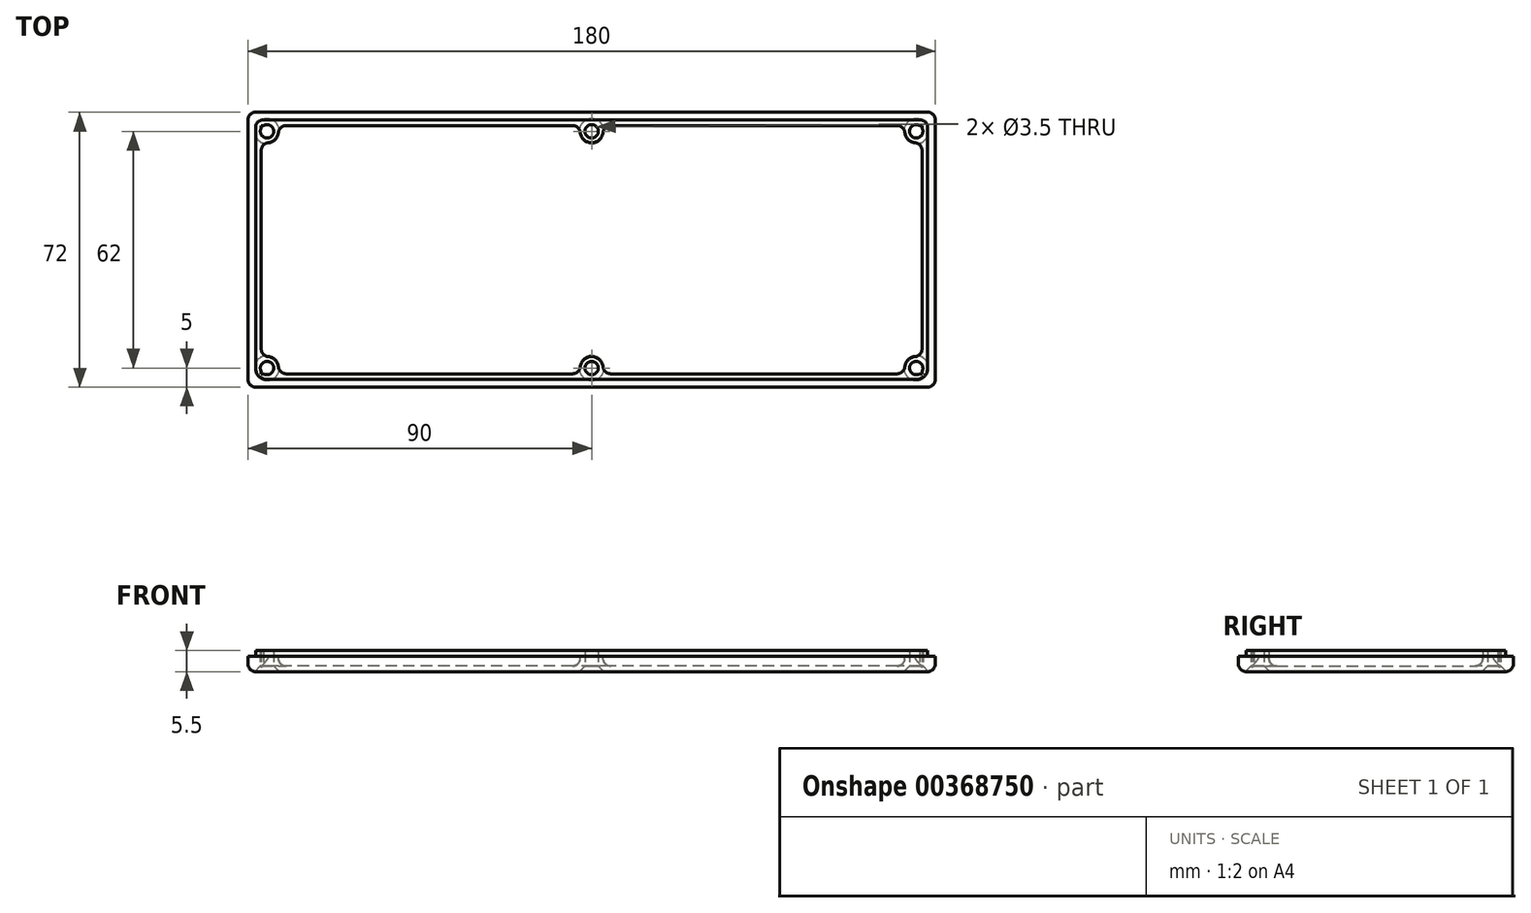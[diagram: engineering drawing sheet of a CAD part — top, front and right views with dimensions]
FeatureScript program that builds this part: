
annotation { "Feature Type Name" : "Feature", "Feature Type Description" : "" }
export const myFeature = defineFeature(function(context is Context, id is Id, definition is map)
    precondition{}
    {
        {
            var Q0;
            Q0=qCreatedBy(makeId("Top.planeOp"),FACE);
            var sketch = newSketch(context, id + "F0", { "sketchPlane" : qUnion([Q0])});
            skLineSegment(sketch, "E0.bottom", {"start": v(-90, 36) * mm, "end": v(90, 36) * mm});
            skLineSegment(sketch, "E0.top", {"start": v(-90, -36) * mm, "end": v(90, -36) * mm});
            skLineSegment(sketch, "E0.left", {"start": v(-90, 36) * mm, "end": v(-90, -36) * mm});
            skLineSegment(sketch, "E0.right", {"start": v(90, 36) * mm, "end": v(90, -36) * mm});
            skPoint(sketch, "E0.middle", {"position": v(0, 0) * mm});
            skLineSegment(sketch, "E1.bottom", {"start": v(-88, 34) * mm, "end": v(88, 34) * mm});
            skLineSegment(sketch, "E1.top", {"start": v(-88, -34) * mm, "end": v(88, -34) * mm});
            skLineSegment(sketch, "E1.left", {"start": v(-88, 34) * mm, "end": v(-88, -34) * mm});
            skLineSegment(sketch, "E1.right", {"start": v(88, 34) * mm, "end": v(88, -34) * mm});
            skLineSegment(sketch, "E2.bottom", {"start": v(-86.5, 32.5) * mm, "end": v(86.5, 32.5) * mm});
            skLineSegment(sketch, "E2.top", {"start": v(-86.5, -32.5) * mm, "end": v(86.5, -32.5) * mm});
            skLineSegment(sketch, "E2.left", {"start": v(-86.5, 32.5) * mm, "end": v(-86.5, -32.5) * mm});
            skLineSegment(sketch, "E2.right", {"start": v(86.5, 32.5) * mm, "end": v(86.5, -32.5) * mm});
            skCircle(sketch, "E3", {"center": v(-85, 31) * mm, "radius": 1.75 * mm});
            skCircle(sketch, "E4.MirrorC", {"center": v(85, 31) * mm, "radius": 1.75 * mm});
            skCircle(sketch, "E5.MirrorC", {"center": v(-85, -31) * mm, "radius": 1.75 * mm});
            skCircle(sketch, "E6.MirrorC", {"center": v(85, -31) * mm, "radius": 1.75 * mm});
            skCircle(sketch, "E7", {"center": v(0, 31) * mm, "radius": 1.75 * mm});
            skCircle(sketch, "E8.MirrorC", {"center": v(0, -31) * mm, "radius": 1.75 * mm});
            skCircle(sketch, "E9", {"center": v(-85, 31) * mm, "radius": 3 * mm});
            skCircle(sketch, "E10.MirrorC", {"center": v(85, 31) * mm, "radius": 3 * mm});
            skCircle(sketch, "E11.MirrorC", {"center": v(-85, -31) * mm, "radius": 3 * mm});
            skCircle(sketch, "E12.MirrorC", {"center": v(85, -31) * mm, "radius": 3 * mm});
            skCircle(sketch, "E13", {"center": v(0, 31) * mm, "radius": 3 * mm});
            skCircle(sketch, "E14.MirrorC", {"center": v(0, -31) * mm, "radius": 3 * mm});
            skSolve(sketch);
        }
        {
            var Q0;
            {var subQ5=sQuery(id+"F0.wireOp",EDGE,"E9");var subQ12=sQuery(id+"F0.wireOp",EDGE,"E2.bottom");var subQ15=makeQuery(id+"F0.imprint","INTERSECT",VERTEX,{"derivedFrom":[subQ12,subQ5]});Q0=makeQuery(id+"F0.imprint","IMPRINT",FACE,{"disambiguationData":[TD([[makeQuery(id+"F0.imprint","IMPRINT",EDGE,{"disambiguationData":[TD([[subQ15,-1.0]])],"derivedFrom":subQ12}),-1.0]])]});}
            var Q1;
            {var subQ0=sQuery(id+"F0.wireOp",EDGE,"E9");var subQ1=sQuery(id+"F0.wireOp",EDGE,"E1.bottom");var subQ2=makeQuery(id+"F0.imprint","INTERSECT",VERTEX,{"derivedFrom":[subQ1,subQ0]});Q1=makeQuery(id+"F0.imprint","IMPRINT",FACE,{"disambiguationData":[TD([[makeQuery(id+"F0.imprint","IMPRINT",EDGE,{"disambiguationData":[TD([[subQ2,-1.0]])],"derivedFrom":subQ1}),-1.0]])]});}
            var Q2;
            Q2=makeQuery(id+"F0.imprint","IMPRINT",FACE,{"disambiguationData":[TD([[makeQuery(id+"F0.imprint","IMPRINT",EDGE,{"derivedFrom":sQuery(id+"F0.wireOp",EDGE,"E0.bottom")}),-1.0]])]});
            var Q3;
            {var subQ0=sQuery(id+"F0.wireOp",EDGE,"E13");var subQ1=sQuery(id+"F0.wireOp",EDGE,"E1.bottom");var subQ2=makeQuery(id+"F0.imprint","INTERSECT",VERTEX,{"derivedFrom":[subQ1,subQ0]});Q3=makeQuery(id+"F0.imprint","IMPRINT",FACE,{"disambiguationData":[TD([[makeQuery(id+"F0.imprint","IMPRINT",EDGE,{"disambiguationData":[TD([[subQ2,-1.0]])],"derivedFrom":subQ1}),-1.0]])]});}
            var Q4;
            {var subQ0=sQuery(id+"F0.wireOp",EDGE,"E13");var subQ1=sQuery(id+"F0.wireOp",EDGE,"E2.bottom");var subQ2=makeQuery(id+"F0.imprint","INTERSECT",VERTEX,{"disambiguationData":[OD(0.0)],"derivedFrom":[subQ1,subQ0]});Q4=makeQuery(id+"F0.imprint","IMPRINT",FACE,{"disambiguationData":[TD([[makeQuery(id+"F0.imprint","IMPRINT",EDGE,{"disambiguationData":[TD([[subQ2,-1.0]])],"derivedFrom":subQ1}),-1.0]])]});}
            var Q5;
            {var subQ0=sQuery(id+"F0.wireOp",EDGE,"E13");var subQ2=sQuery(id+"F0.wireOp",EDGE,"E2.bottom");var subQ7=makeQuery(id+"F0.imprint","INTERSECT",VERTEX,{"disambiguationData":[OD(0.0)],"derivedFrom":[subQ2,subQ0]});Q5=makeQuery(id+"F0.imprint","IMPRINT",FACE,{"disambiguationData":[TD([[makeQuery(id+"F0.imprint","IMPRINT",EDGE,{"disambiguationData":[TD([[subQ7,-1.0]])],"derivedFrom":subQ2}),1.0]])]});}
            var Q6;
            {var subQ0=sQuery(id+"F0.wireOp",EDGE,"E9");var subQ1=sQuery(id+"F0.wireOp",EDGE,"E1.left");var subQ2=makeQuery(id+"F0.imprint","INTERSECT",VERTEX,{"derivedFrom":[subQ1,subQ0]});Q6=makeQuery(id+"F0.imprint","IMPRINT",FACE,{"disambiguationData":[TD([[makeQuery(id+"F0.imprint","IMPRINT",EDGE,{"disambiguationData":[TD([[subQ2,-1.0]])],"derivedFrom":subQ1}),1.0]])]});}
            var Q7;
            {var subQ1=sQuery(id+"F0.wireOp",EDGE,"E2.left");var subQ5=sQuery(id+"F0.wireOp",EDGE,"E2.bottom");var subQ10=makeQuery(id+"F0.imprint","INTERSECT",VERTEX,{"derivedFrom":[subQ5,subQ1]});Q7=makeQuery(id+"F0.imprint","IMPRINT",FACE,{"disambiguationData":[TD([[makeQuery(id+"F0.imprint","IMPRINT",EDGE,{"disambiguationData":[TD([[subQ10,-1.0]])],"derivedFrom":subQ5}),1.0]])]});}
            var Q8;
            {var subQ0=sQuery(id+"F0.wireOp",EDGE,"E3");var subQ1=sQuery(id+"F0.wireOp",EDGE,"E2.bottom");var subQ2=makeQuery(id+"F0.imprint","INTERSECT",VERTEX,{"disambiguationData":[OD(1.0)],"derivedFrom":[subQ1,subQ0]});Q8=makeQuery(id+"F0.imprint","IMPRINT",FACE,{"disambiguationData":[TD([[makeQuery(id+"F0.imprint","IMPRINT",EDGE,{"disambiguationData":[TD([[subQ2,-1.0]])],"derivedFrom":subQ1}),-1.0]])]});}
            var Q9;
            {var subQ0=sQuery(id+"F0.wireOp",EDGE,"E1.left");var subQ1=sQuery(id+"F0.wireOp",EDGE,"E1.bottom");var subQ2=makeQuery(id+"F0.imprint","INTERSECT",VERTEX,{"derivedFrom":[subQ1,subQ0]});Q9=makeQuery(id+"F0.imprint","IMPRINT",FACE,{"disambiguationData":[TD([[makeQuery(id+"F0.imprint","IMPRINT",EDGE,{"disambiguationData":[TD([[subQ2,-1.0]])],"derivedFrom":subQ1}),-1.0]])]});}
            var Q10;
            {var subQ0=sQuery(id+"F0.wireOp",EDGE,"E5.MirrorC");var subQ1=sQuery(id+"F0.wireOp",EDGE,"E2.top");var subQ2=makeQuery(id+"F0.imprint","INTERSECT",VERTEX,{"disambiguationData":[OD(1.0)],"derivedFrom":[subQ1,subQ0]});Q10=makeQuery(id+"F0.imprint","IMPRINT",FACE,{"disambiguationData":[TD([[makeQuery(id+"F0.imprint","IMPRINT",EDGE,{"disambiguationData":[TD([[subQ2,-1.0]])],"derivedFrom":subQ1}),1.0]])]});}
            var Q11;
            {var subQ0=sQuery(id+"F0.wireOp",EDGE,"E2.left");var subQ1=sQuery(id+"F0.wireOp",EDGE,"E2.top");var subQ2=makeQuery(id+"F0.imprint","INTERSECT",VERTEX,{"derivedFrom":[subQ1,subQ0]});Q11=makeQuery(id+"F0.imprint","IMPRINT",FACE,{"disambiguationData":[TD([[makeQuery(id+"F0.imprint","IMPRINT",EDGE,{"disambiguationData":[TD([[subQ2,-1.0]])],"derivedFrom":subQ1}),-1.0]])]});}
            var Q12;
            {var subQ0=sQuery(id+"F0.wireOp",EDGE,"E1.left");var subQ1=sQuery(id+"F0.wireOp",EDGE,"E1.top");var subQ2=makeQuery(id+"F0.imprint","INTERSECT",VERTEX,{"derivedFrom":[subQ1,subQ0]});Q12=makeQuery(id+"F0.imprint","IMPRINT",FACE,{"disambiguationData":[TD([[makeQuery(id+"F0.imprint","IMPRINT",EDGE,{"disambiguationData":[TD([[subQ2,-1.0]])],"derivedFrom":subQ1}),1.0]])]});}
            var Q13;
            {var subQ0=sQuery(id+"F0.wireOp",EDGE,"E11.MirrorC");var subQ1=sQuery(id+"F0.wireOp",EDGE,"E1.top");var subQ2=makeQuery(id+"F0.imprint","INTERSECT",VERTEX,{"derivedFrom":[subQ1,subQ0]});Q13=makeQuery(id+"F0.imprint","IMPRINT",FACE,{"disambiguationData":[TD([[makeQuery(id+"F0.imprint","IMPRINT",EDGE,{"disambiguationData":[TD([[subQ2,-1.0]])],"derivedFrom":subQ1}),1.0]])]});}
            var Q14;
            {var subQ1=sQuery(id+"F0.wireOp",EDGE,"E2.top");var subQ4=sQuery(id+"F0.wireOp",EDGE,"E14.MirrorC");var subQ6=makeQuery(id+"F0.imprint","INTERSECT",VERTEX,{"disambiguationData":[OD(0.0)],"derivedFrom":[subQ1,subQ4]});Q14=makeQuery(id+"F0.imprint","IMPRINT",FACE,{"disambiguationData":[TD([[makeQuery(id+"F0.imprint","IMPRINT",EDGE,{"disambiguationData":[TD([[subQ6,-1.0]])],"derivedFrom":subQ1}),-1.0]])]});}
            var Q15;
            {var subQ0=sQuery(id+"F0.wireOp",EDGE,"E14.MirrorC");var subQ1=sQuery(id+"F0.wireOp",EDGE,"E2.top");var subQ2=makeQuery(id+"F0.imprint","INTERSECT",VERTEX,{"disambiguationData":[OD(0.0)],"derivedFrom":[subQ1,subQ0]});Q15=makeQuery(id+"F0.imprint","IMPRINT",FACE,{"disambiguationData":[TD([[makeQuery(id+"F0.imprint","IMPRINT",EDGE,{"disambiguationData":[TD([[subQ2,-1.0]])],"derivedFrom":subQ1}),1.0]])]});}
            var Q16;
            {var subQ0=sQuery(id+"F0.wireOp",EDGE,"E14.MirrorC");var subQ1=sQuery(id+"F0.wireOp",EDGE,"E1.top");var subQ2=makeQuery(id+"F0.imprint","INTERSECT",VERTEX,{"derivedFrom":[subQ1,subQ0]});Q16=makeQuery(id+"F0.imprint","IMPRINT",FACE,{"disambiguationData":[TD([[makeQuery(id+"F0.imprint","IMPRINT",EDGE,{"disambiguationData":[TD([[subQ2,-1.0]])],"derivedFrom":subQ1}),1.0]])]});}
            var Q17;
            {var subQ1=sQuery(id+"F0.wireOp",EDGE,"E2.top");var subQ5=sQuery(id+"F0.wireOp",EDGE,"E12.MirrorC");var subQ7=makeQuery(id+"F0.imprint","INTERSECT",VERTEX,{"derivedFrom":[subQ1,subQ5]});Q17=makeQuery(id+"F0.imprint","IMPRINT",FACE,{"disambiguationData":[TD([[makeQuery(id+"F0.imprint","IMPRINT",EDGE,{"disambiguationData":[TD([[subQ7,-1.0]])],"derivedFrom":subQ1}),-1.0]])]});}
            var Q18;
            {var subQ0=sQuery(id+"F0.wireOp",EDGE,"E10.MirrorC");var subQ1=sQuery(id+"F0.wireOp",EDGE,"E1.right");var subQ2=makeQuery(id+"F0.imprint","INTERSECT",VERTEX,{"derivedFrom":[subQ1,subQ0]});Q18=makeQuery(id+"F0.imprint","IMPRINT",FACE,{"disambiguationData":[TD([[makeQuery(id+"F0.imprint","IMPRINT",EDGE,{"disambiguationData":[TD([[subQ2,-1.0]])],"derivedFrom":subQ1}),-1.0]])]});}
            var Q19;
            {var subQ0=sQuery(id+"F0.wireOp",EDGE,"E12.MirrorC");var subQ1=sQuery(id+"F0.wireOp",EDGE,"E2.top");var subQ2=makeQuery(id+"F0.imprint","INTERSECT",VERTEX,{"derivedFrom":[subQ1,subQ0]});Q19=makeQuery(id+"F0.imprint","IMPRINT",FACE,{"disambiguationData":[TD([[makeQuery(id+"F0.imprint","IMPRINT",EDGE,{"disambiguationData":[TD([[subQ2,-1.0]])],"derivedFrom":subQ1}),1.0]])]});}
            var Q20;
            {var subQ0=sQuery(id+"F0.wireOp",EDGE,"E10.MirrorC");var subQ1=sQuery(id+"F0.wireOp",EDGE,"E2.bottom");var subQ2=makeQuery(id+"F0.imprint","INTERSECT",VERTEX,{"derivedFrom":[subQ1,subQ0]});Q20=makeQuery(id+"F0.imprint","IMPRINT",FACE,{"disambiguationData":[TD([[makeQuery(id+"F0.imprint","IMPRINT",EDGE,{"disambiguationData":[TD([[subQ2,-1.0]])],"derivedFrom":subQ1}),-1.0]])]});}
            var Q21;
            {var subQ3=sQuery(id+"F0.wireOp",EDGE,"E10.MirrorC");var subQ6=sQuery(id+"F0.wireOp",EDGE,"E2.bottom");var subQ11=makeQuery(id+"F0.imprint","INTERSECT",VERTEX,{"derivedFrom":[subQ6,subQ3]});Q21=makeQuery(id+"F0.imprint","IMPRINT",FACE,{"disambiguationData":[TD([[makeQuery(id+"F0.imprint","IMPRINT",EDGE,{"disambiguationData":[TD([[subQ11,-1.0]])],"derivedFrom":subQ6}),1.0]])]});}
            var Q22;
            {var subQ0=sQuery(id+"F0.wireOp",EDGE,"E1.right");var subQ1=sQuery(id+"F0.wireOp",EDGE,"E1.bottom");var subQ2=makeQuery(id+"F0.imprint","INTERSECT",VERTEX,{"derivedFrom":[subQ1,subQ0]});Q22=makeQuery(id+"F0.imprint","IMPRINT",FACE,{"disambiguationData":[TD([[makeQuery(id+"F0.imprint","IMPRINT",EDGE,{"disambiguationData":[TD([[subQ2,1.0]])],"derivedFrom":subQ1}),-1.0]])]});}
            var Q23;
            {var subQ0=sQuery(id+"F0.wireOp",EDGE,"E1.right");var subQ1=sQuery(id+"F0.wireOp",EDGE,"E1.top");var subQ2=makeQuery(id+"F0.imprint","INTERSECT",VERTEX,{"derivedFrom":[subQ1,subQ0]});Q23=makeQuery(id+"F0.imprint","IMPRINT",FACE,{"disambiguationData":[TD([[makeQuery(id+"F0.imprint","IMPRINT",EDGE,{"disambiguationData":[TD([[subQ2,1.0]])],"derivedFrom":subQ1}),1.0]])]});}
            extrude(context, id + "F1", {"entities" : qUnion([Q0, Q1, Q2, Q3, Q4, Q5, Q6, Q7, Q8, Q9, Q10, Q11, Q12, Q13, Q14, Q15, Q16, Q17, Q18, Q19, Q20, Q21, Q22, Q23]), "depth" : 1.5 * mm, "offsetDistance" : 25 * mm});
        }
        {
            var Q0;
            Q0=makeQuery(id+"F0.imprint","IMPRINT",FACE,{"disambiguationData":[TD([[makeQuery(id+"F0.imprint","IMPRINT",EDGE,{"derivedFrom":sQuery(id+"F0.wireOp",EDGE,"E0.bottom")}),-1.0]])]});
            var Q1;
            {var subQ0=sQuery(id+"F0.wireOp",EDGE,"E1.left");var subQ1=sQuery(id+"F0.wireOp",EDGE,"E1.bottom");var subQ2=makeQuery(id+"F0.imprint","INTERSECT",VERTEX,{"derivedFrom":[subQ1,subQ0]});Q1=makeQuery(id+"F0.imprint","IMPRINT",FACE,{"disambiguationData":[TD([[makeQuery(id+"F0.imprint","IMPRINT",EDGE,{"disambiguationData":[TD([[subQ2,-1.0]])],"derivedFrom":subQ1}),-1.0]])]});}
            var Q2;
            {var subQ0=sQuery(id+"F0.wireOp",EDGE,"E1.left");var subQ1=sQuery(id+"F0.wireOp",EDGE,"E1.top");var subQ2=makeQuery(id+"F0.imprint","INTERSECT",VERTEX,{"derivedFrom":[subQ1,subQ0]});Q2=makeQuery(id+"F0.imprint","IMPRINT",FACE,{"disambiguationData":[TD([[makeQuery(id+"F0.imprint","IMPRINT",EDGE,{"disambiguationData":[TD([[subQ2,-1.0]])],"derivedFrom":subQ1}),1.0]])]});}
            var Q3;
            {var subQ0=sQuery(id+"F0.wireOp",EDGE,"E1.right");var subQ1=sQuery(id+"F0.wireOp",EDGE,"E1.top");var subQ2=makeQuery(id+"F0.imprint","INTERSECT",VERTEX,{"derivedFrom":[subQ1,subQ0]});Q3=makeQuery(id+"F0.imprint","IMPRINT",FACE,{"disambiguationData":[TD([[makeQuery(id+"F0.imprint","IMPRINT",EDGE,{"disambiguationData":[TD([[subQ2,1.0]])],"derivedFrom":subQ1}),1.0]])]});}
            var Q4;
            {var subQ0=sQuery(id+"F0.wireOp",EDGE,"E1.right");var subQ1=sQuery(id+"F0.wireOp",EDGE,"E1.bottom");var subQ2=makeQuery(id+"F0.imprint","INTERSECT",VERTEX,{"derivedFrom":[subQ1,subQ0]});Q4=makeQuery(id+"F0.imprint","IMPRINT",FACE,{"disambiguationData":[TD([[makeQuery(id+"F0.imprint","IMPRINT",EDGE,{"disambiguationData":[TD([[subQ2,1.0]])],"derivedFrom":subQ1}),-1.0]])]});}
            extrude(context, id + "F2", {"entities" : qUnion([Q0, Q1, Q2, Q3, Q4]), "operationType" : NewBodyOperationType.ADD, "depth" : 4 * mm, "offsetDistance" : 25 * mm});
        }
        {
            var Q0;
            Q0=makeQuery(id+"F0.imprint","IMPRINT",FACE,{"disambiguationData":[TD([[makeQuery(id+"F0.imprint","IMPRINT",EDGE,{"derivedFrom":sQuery(id+"F0.wireOp",EDGE,"E1.bottom")}),-1.0]])]});
            var Q1;
            {var subQ0=sQuery(id+"F0.wireOp",EDGE,"E10.MirrorC");var subQ1=sQuery(id+"F0.wireOp",EDGE,"E2.bottom");var subQ2=makeQuery(id+"F0.imprint","INTERSECT",VERTEX,{"derivedFrom":[subQ1,subQ0]});Q1=makeQuery(id+"F0.imprint","IMPRINT",FACE,{"disambiguationData":[TD([[makeQuery(id+"F0.imprint","IMPRINT",EDGE,{"disambiguationData":[TD([[subQ2,-1.0]])],"derivedFrom":subQ1}),-1.0]])]});}
            var Q2;
            {var subQ3=sQuery(id+"F0.wireOp",EDGE,"E10.MirrorC");var subQ6=sQuery(id+"F0.wireOp",EDGE,"E2.bottom");var subQ11=makeQuery(id+"F0.imprint","INTERSECT",VERTEX,{"derivedFrom":[subQ6,subQ3]});Q2=makeQuery(id+"F0.imprint","IMPRINT",FACE,{"disambiguationData":[TD([[makeQuery(id+"F0.imprint","IMPRINT",EDGE,{"disambiguationData":[TD([[subQ11,-1.0]])],"derivedFrom":subQ6}),1.0]])]});}
            var Q3;
            {var subQ0=sQuery(id+"F0.wireOp",EDGE,"E10.MirrorC");var subQ1=sQuery(id+"F0.wireOp",EDGE,"E1.right");var subQ2=makeQuery(id+"F0.imprint","INTERSECT",VERTEX,{"derivedFrom":[subQ1,subQ0]});Q3=makeQuery(id+"F0.imprint","IMPRINT",FACE,{"disambiguationData":[TD([[makeQuery(id+"F0.imprint","IMPRINT",EDGE,{"disambiguationData":[TD([[subQ2,-1.0]])],"derivedFrom":subQ1}),-1.0]])]});}
            var Q4;
            {var subQ0=sQuery(id+"F0.wireOp",EDGE,"E13");var subQ1=sQuery(id+"F0.wireOp",EDGE,"E1.bottom");var subQ2=makeQuery(id+"F0.imprint","INTERSECT",VERTEX,{"derivedFrom":[subQ1,subQ0]});Q4=makeQuery(id+"F0.imprint","IMPRINT",FACE,{"disambiguationData":[TD([[makeQuery(id+"F0.imprint","IMPRINT",EDGE,{"disambiguationData":[TD([[subQ2,-1.0]])],"derivedFrom":subQ1}),-1.0]])]});}
            var Q5;
            {var subQ0=sQuery(id+"F0.wireOp",EDGE,"E13");var subQ2=sQuery(id+"F0.wireOp",EDGE,"E2.bottom");var subQ7=makeQuery(id+"F0.imprint","INTERSECT",VERTEX,{"disambiguationData":[OD(0.0)],"derivedFrom":[subQ2,subQ0]});Q5=makeQuery(id+"F0.imprint","IMPRINT",FACE,{"disambiguationData":[TD([[makeQuery(id+"F0.imprint","IMPRINT",EDGE,{"disambiguationData":[TD([[subQ7,-1.0]])],"derivedFrom":subQ2}),1.0]])]});}
            var Q6;
            {var subQ0=sQuery(id+"F0.wireOp",EDGE,"E13");var subQ1=sQuery(id+"F0.wireOp",EDGE,"E2.bottom");var subQ2=makeQuery(id+"F0.imprint","INTERSECT",VERTEX,{"disambiguationData":[OD(0.0)],"derivedFrom":[subQ1,subQ0]});Q6=makeQuery(id+"F0.imprint","IMPRINT",FACE,{"disambiguationData":[TD([[makeQuery(id+"F0.imprint","IMPRINT",EDGE,{"disambiguationData":[TD([[subQ2,-1.0]])],"derivedFrom":subQ1}),-1.0]])]});}
            var Q7;
            {var subQ0=sQuery(id+"F0.wireOp",EDGE,"E9");var subQ1=sQuery(id+"F0.wireOp",EDGE,"E1.bottom");var subQ2=makeQuery(id+"F0.imprint","INTERSECT",VERTEX,{"derivedFrom":[subQ1,subQ0]});Q7=makeQuery(id+"F0.imprint","IMPRINT",FACE,{"disambiguationData":[TD([[makeQuery(id+"F0.imprint","IMPRINT",EDGE,{"disambiguationData":[TD([[subQ2,-1.0]])],"derivedFrom":subQ1}),-1.0]])]});}
            var Q8;
            {var subQ0=sQuery(id+"F0.wireOp",EDGE,"E12.MirrorC");var subQ1=sQuery(id+"F0.wireOp",EDGE,"E2.top");var subQ2=makeQuery(id+"F0.imprint","INTERSECT",VERTEX,{"derivedFrom":[subQ1,subQ0]});Q8=makeQuery(id+"F0.imprint","IMPRINT",FACE,{"disambiguationData":[TD([[makeQuery(id+"F0.imprint","IMPRINT",EDGE,{"disambiguationData":[TD([[subQ2,-1.0]])],"derivedFrom":subQ1}),1.0]])]});}
            var Q9;
            {var subQ1=sQuery(id+"F0.wireOp",EDGE,"E2.top");var subQ5=sQuery(id+"F0.wireOp",EDGE,"E12.MirrorC");var subQ7=makeQuery(id+"F0.imprint","INTERSECT",VERTEX,{"derivedFrom":[subQ1,subQ5]});Q9=makeQuery(id+"F0.imprint","IMPRINT",FACE,{"disambiguationData":[TD([[makeQuery(id+"F0.imprint","IMPRINT",EDGE,{"disambiguationData":[TD([[subQ7,-1.0]])],"derivedFrom":subQ1}),-1.0]])]});}
            var Q10;
            {var subQ0=sQuery(id+"F0.wireOp",EDGE,"E14.MirrorC");var subQ1=sQuery(id+"F0.wireOp",EDGE,"E1.top");var subQ2=makeQuery(id+"F0.imprint","INTERSECT",VERTEX,{"derivedFrom":[subQ1,subQ0]});Q10=makeQuery(id+"F0.imprint","IMPRINT",FACE,{"disambiguationData":[TD([[makeQuery(id+"F0.imprint","IMPRINT",EDGE,{"disambiguationData":[TD([[subQ2,-1.0]])],"derivedFrom":subQ1}),1.0]])]});}
            var Q11;
            {var subQ0=sQuery(id+"F0.wireOp",EDGE,"E14.MirrorC");var subQ1=sQuery(id+"F0.wireOp",EDGE,"E2.top");var subQ2=makeQuery(id+"F0.imprint","INTERSECT",VERTEX,{"disambiguationData":[OD(0.0)],"derivedFrom":[subQ1,subQ0]});Q11=makeQuery(id+"F0.imprint","IMPRINT",FACE,{"disambiguationData":[TD([[makeQuery(id+"F0.imprint","IMPRINT",EDGE,{"disambiguationData":[TD([[subQ2,-1.0]])],"derivedFrom":subQ1}),1.0]])]});}
            var Q12;
            {var subQ1=sQuery(id+"F0.wireOp",EDGE,"E2.top");var subQ4=sQuery(id+"F0.wireOp",EDGE,"E14.MirrorC");var subQ6=makeQuery(id+"F0.imprint","INTERSECT",VERTEX,{"disambiguationData":[OD(0.0)],"derivedFrom":[subQ1,subQ4]});Q12=makeQuery(id+"F0.imprint","IMPRINT",FACE,{"disambiguationData":[TD([[makeQuery(id+"F0.imprint","IMPRINT",EDGE,{"disambiguationData":[TD([[subQ6,-1.0]])],"derivedFrom":subQ1}),-1.0]])]});}
            var Q13;
            {var subQ0=sQuery(id+"F0.wireOp",EDGE,"E11.MirrorC");var subQ1=sQuery(id+"F0.wireOp",EDGE,"E1.top");var subQ2=makeQuery(id+"F0.imprint","INTERSECT",VERTEX,{"derivedFrom":[subQ1,subQ0]});Q13=makeQuery(id+"F0.imprint","IMPRINT",FACE,{"disambiguationData":[TD([[makeQuery(id+"F0.imprint","IMPRINT",EDGE,{"disambiguationData":[TD([[subQ2,-1.0]])],"derivedFrom":subQ1}),1.0]])]});}
            var Q14;
            {var subQ0=sQuery(id+"F0.wireOp",EDGE,"E9");var subQ1=sQuery(id+"F0.wireOp",EDGE,"E1.left");var subQ2=makeQuery(id+"F0.imprint","INTERSECT",VERTEX,{"derivedFrom":[subQ1,subQ0]});Q14=makeQuery(id+"F0.imprint","IMPRINT",FACE,{"disambiguationData":[TD([[makeQuery(id+"F0.imprint","IMPRINT",EDGE,{"disambiguationData":[TD([[subQ2,-1.0]])],"derivedFrom":subQ1}),1.0]])]});}
            var Q15;
            {var subQ0=sQuery(id+"F0.wireOp",EDGE,"E5.MirrorC");var subQ1=sQuery(id+"F0.wireOp",EDGE,"E2.top");var subQ2=makeQuery(id+"F0.imprint","INTERSECT",VERTEX,{"disambiguationData":[OD(1.0)],"derivedFrom":[subQ1,subQ0]});Q15=makeQuery(id+"F0.imprint","IMPRINT",FACE,{"disambiguationData":[TD([[makeQuery(id+"F0.imprint","IMPRINT",EDGE,{"disambiguationData":[TD([[subQ2,-1.0]])],"derivedFrom":subQ1}),1.0]])]});}
            var Q16;
            {var subQ0=sQuery(id+"F0.wireOp",EDGE,"E2.left");var subQ1=sQuery(id+"F0.wireOp",EDGE,"E2.top");var subQ2=makeQuery(id+"F0.imprint","INTERSECT",VERTEX,{"derivedFrom":[subQ1,subQ0]});Q16=makeQuery(id+"F0.imprint","IMPRINT",FACE,{"disambiguationData":[TD([[makeQuery(id+"F0.imprint","IMPRINT",EDGE,{"disambiguationData":[TD([[subQ2,-1.0]])],"derivedFrom":subQ1}),-1.0]])]});}
            var Q17;
            {var subQ0=sQuery(id+"F0.wireOp",EDGE,"E3");var subQ1=sQuery(id+"F0.wireOp",EDGE,"E2.bottom");var subQ2=makeQuery(id+"F0.imprint","INTERSECT",VERTEX,{"disambiguationData":[OD(1.0)],"derivedFrom":[subQ1,subQ0]});Q17=makeQuery(id+"F0.imprint","IMPRINT",FACE,{"disambiguationData":[TD([[makeQuery(id+"F0.imprint","IMPRINT",EDGE,{"disambiguationData":[TD([[subQ2,-1.0]])],"derivedFrom":subQ1}),-1.0]])]});}
            var Q18;
            {var subQ1=sQuery(id+"F0.wireOp",EDGE,"E2.left");var subQ5=sQuery(id+"F0.wireOp",EDGE,"E2.bottom");var subQ10=makeQuery(id+"F0.imprint","INTERSECT",VERTEX,{"derivedFrom":[subQ5,subQ1]});Q18=makeQuery(id+"F0.imprint","IMPRINT",FACE,{"disambiguationData":[TD([[makeQuery(id+"F0.imprint","IMPRINT",EDGE,{"disambiguationData":[TD([[subQ10,-1.0]])],"derivedFrom":subQ5}),1.0]])]});}
            extrude(context, id + "F3", {"entities" : qUnion([Q0, Q1, Q2, Q3, Q4, Q5, Q6, Q7, Q8, Q9, Q10, Q11, Q12, Q13, Q14, Q15, Q16, Q17, Q18]), "operationType" : NewBodyOperationType.ADD, "depth" : 5.5 * mm, "offsetDistance" : 25 * mm});
        }
        {
            var Q0;
            Q0=makeQuery(id+"F1.opExtrude","CAP_EDGE",EDGE,{"disambiguationData":[OSD([sQuery(id+"F0.wireOp",EDGE,"E0.top")])],"isStart":true});
            var Q1;
            Q1=makeQuery(id+"F1.opExtrude","CAP_EDGE",EDGE,{"disambiguationData":[OSD([sQuery(id+"F0.wireOp",EDGE,"E0.left")])],"isStart":true});
            var Q2;
            Q2=makeQuery(id+"F1.opExtrude","CAP_EDGE",EDGE,{"disambiguationData":[OSD([sQuery(id+"F0.wireOp",EDGE,"E0.bottom")])],"isStart":true});
            var Q3;
            Q3=makeQuery(id+"F1.opExtrude","CAP_EDGE",EDGE,{"disambiguationData":[OSD([sQuery(id+"F0.wireOp",EDGE,"E0.right")])],"isStart":true});
            var Q4;
            {var subQ0=sQuery(id+"F0.wireOp",EDGE,"E0.right");var subQ1=sQuery(id+"F0.wireOp",EDGE,"E0.top");Q4=makeQuery(id+"F2.boolean.opBoolean","MERGE",EDGE,{"derivedFrom":[makeQuery(id+"F1.opExtrude","SWEPT_EDGE",EDGE,{"disambiguationData":[OSD([subQ1,subQ0])]}),makeQuery(id+"F2.opExtrude","SWEPT_EDGE",EDGE,{"disambiguationData":[OSD([subQ1,subQ0])]})]});}
            var Q5;
            {var subQ0=sQuery(id+"F0.wireOp",EDGE,"E0.right");var subQ1=sQuery(id+"F0.wireOp",EDGE,"E0.bottom");Q5=makeQuery(id+"F2.boolean.opBoolean","MERGE",EDGE,{"derivedFrom":[makeQuery(id+"F1.opExtrude","SWEPT_EDGE",EDGE,{"disambiguationData":[OSD([subQ1,subQ0])]}),makeQuery(id+"F2.opExtrude","SWEPT_EDGE",EDGE,{"disambiguationData":[OSD([subQ1,subQ0])]})]});}
            var Q6;
            {var subQ0=sQuery(id+"F0.wireOp",EDGE,"E0.left");var subQ1=sQuery(id+"F0.wireOp",EDGE,"E0.bottom");Q6=makeQuery(id+"F2.boolean.opBoolean","MERGE",EDGE,{"derivedFrom":[makeQuery(id+"F1.opExtrude","SWEPT_EDGE",EDGE,{"disambiguationData":[OSD([subQ1,subQ0])]}),makeQuery(id+"F2.opExtrude","SWEPT_EDGE",EDGE,{"disambiguationData":[OSD([subQ1,subQ0])]})]});}
            var Q7;
            {var subQ0=sQuery(id+"F0.wireOp",EDGE,"E0.left");var subQ1=sQuery(id+"F0.wireOp",EDGE,"E0.top");Q7=makeQuery(id+"F2.boolean.opBoolean","MERGE",EDGE,{"derivedFrom":[makeQuery(id+"F1.opExtrude","SWEPT_EDGE",EDGE,{"disambiguationData":[OSD([subQ1,subQ0])]}),makeQuery(id+"F2.opExtrude","SWEPT_EDGE",EDGE,{"disambiguationData":[OSD([subQ1,subQ0])]})]});}
            var Q8;
            Q8=makeQuery(id+"F3.opExtrude","SWEPT_EDGE",EDGE,{"disambiguationData":[OSD([sQuery(id+"F0.wireOp",EDGE,"E1.bottom"),sQuery(id+"F0.wireOp",EDGE,"E1.right")])]});
            var Q9;
            Q9=makeQuery(id+"F3.opExtrude","SWEPT_EDGE",EDGE,{"disambiguationData":[OSD([sQuery(id+"F0.wireOp",EDGE,"E1.bottom"),sQuery(id+"F0.wireOp",EDGE,"E1.left")])]});
            var Q10;
            Q10=makeQuery(id+"F3.opExtrude","SWEPT_EDGE",EDGE,{"disambiguationData":[OSD([sQuery(id+"F0.wireOp",EDGE,"E2.bottom"),sQuery(id+"F0.wireOp",EDGE,"E9")])]});
            var Q11;
            Q11=makeQuery(id+"F3.opExtrude","SWEPT_EDGE",EDGE,{"disambiguationData":[OSD([sQuery(id+"F0.wireOp",EDGE,"E2.left"),sQuery(id+"F0.wireOp",EDGE,"E9")])]});
            var Q12;
            {var subQ0=sQuery(id+"F0.wireOp",EDGE,"E13");var subQ1=sQuery(id+"F0.wireOp",EDGE,"E2.bottom");Q12=makeQuery(id+"F3.opExtrude","SWEPT_EDGE",EDGE,{"disambiguationData":[OSD([subQ1,subQ0]),TDD([makeQuery(id+"F0.imprint","INTERSECT",VERTEX,{"disambiguationData":[OD(1.0)],"derivedFrom":[subQ1,subQ0]})])]});}
            var Q13;
            {var subQ0=sQuery(id+"F0.wireOp",EDGE,"E13");var subQ1=sQuery(id+"F0.wireOp",EDGE,"E2.bottom");Q13=makeQuery(id+"F3.opExtrude","SWEPT_EDGE",EDGE,{"disambiguationData":[OSD([subQ1,subQ0]),TDD([makeQuery(id+"F0.imprint","INTERSECT",VERTEX,{"disambiguationData":[OD(0.0)],"derivedFrom":[subQ1,subQ0]})])]});}
            var Q14;
            Q14=makeQuery(id+"F3.opExtrude","SWEPT_EDGE",EDGE,{"disambiguationData":[OSD([sQuery(id+"F0.wireOp",EDGE,"E2.bottom"),sQuery(id+"F0.wireOp",EDGE,"E10.MirrorC")])]});
            var Q15;
            Q15=makeQuery(id+"F3.opExtrude","SWEPT_EDGE",EDGE,{"disambiguationData":[OSD([sQuery(id+"F0.wireOp",EDGE,"E2.right"),sQuery(id+"F0.wireOp",EDGE,"E10.MirrorC")])]});
            var Q16;
            Q16=makeQuery(id+"F3.opExtrude","SWEPT_EDGE",EDGE,{"disambiguationData":[OSD([sQuery(id+"F0.wireOp",EDGE,"E2.right"),sQuery(id+"F0.wireOp",EDGE,"E12.MirrorC")])]});
            var Q17;
            Q17=makeQuery(id+"F3.opExtrude","SWEPT_EDGE",EDGE,{"disambiguationData":[OSD([sQuery(id+"F0.wireOp",EDGE,"E2.top"),sQuery(id+"F0.wireOp",EDGE,"E12.MirrorC")])]});
            var Q18;
            {var subQ0=sQuery(id+"F0.wireOp",EDGE,"E12.MirrorC");var subQ1=sQuery(id+"F0.wireOp",EDGE,"E2.top");var subQ2=sQuery(id+"F0.wireOp",EDGE,"E2.right");Q18=makeQuery(id+"F3.boolean.opBoolean","INTERSECT",EDGE,{"derivedFrom":[makeQuery(id+"F1.opExtrude","CAP_FACE",FACE,{"disambiguationData":[OSD([sQuery(id+"F0.wireOp",EDGE,"E0.bottom"),sQuery(id+"F0.wireOp",EDGE,"E0.top"),sQuery(id+"F0.wireOp",EDGE,"E0.left"),sQuery(id+"F0.wireOp",EDGE,"E0.right"),sQuery(id+"F0.wireOp",EDGE,"E2.bottom"),subQ1,sQuery(id+"F0.wireOp",EDGE,"E2.left"),subQ2,sQuery(id+"F0.wireOp",EDGE,"E3"),sQuery(id+"F0.wireOp",EDGE,"E4.MirrorC"),sQuery(id+"F0.wireOp",EDGE,"E5.MirrorC"),sQuery(id+"F0.wireOp",EDGE,"E6.MirrorC"),sQuery(id+"F0.wireOp",EDGE,"E7"),sQuery(id+"F0.wireOp",EDGE,"E8.MirrorC")])],"isStart":false}),makeQuery(id+"F3.opExtrude","SWEPT_FACE",FACE,{"disambiguationData":[OSD([subQ0]),TDD([makeQuery(id+"F0.imprint","IMPRINT",EDGE,{"disambiguationData":[TD([[makeQuery(id+"F0.imprint","INTERSECT",VERTEX,{"derivedFrom":[subQ1,subQ0]}),1.0]])],"derivedFrom":subQ0})])]})]});}
            var Q19;
            Q19=makeQuery(id+"F3.boolean.opBoolean","INTERSECT",EDGE,{"derivedFrom":[makeQuery(id+"F1.opExtrude","CAP_FACE",FACE,{"disambiguationData":[OSD([sQuery(id+"F0.wireOp",EDGE,"E0.bottom"),sQuery(id+"F0.wireOp",EDGE,"E0.top"),sQuery(id+"F0.wireOp",EDGE,"E0.left"),sQuery(id+"F0.wireOp",EDGE,"E0.right"),sQuery(id+"F0.wireOp",EDGE,"E2.bottom"),sQuery(id+"F0.wireOp",EDGE,"E2.top"),sQuery(id+"F0.wireOp",EDGE,"E2.left"),sQuery(id+"F0.wireOp",EDGE,"E2.right"),sQuery(id+"F0.wireOp",EDGE,"E3"),sQuery(id+"F0.wireOp",EDGE,"E4.MirrorC"),sQuery(id+"F0.wireOp",EDGE,"E5.MirrorC"),sQuery(id+"F0.wireOp",EDGE,"E6.MirrorC"),sQuery(id+"F0.wireOp",EDGE,"E7"),sQuery(id+"F0.wireOp",EDGE,"E8.MirrorC")])],"isStart":false}),makeQuery(id+"F3.opExtrude","SWEPT_FACE",FACE,{"disambiguationData":[OSD([sQuery(id+"F0.wireOp",EDGE,"E10.MirrorC")])]})]});
            var Q20;
            Q20=makeQuery(id+"F3.boolean.opBoolean","INTERSECT",EDGE,{"derivedFrom":[makeQuery(id+"F1.opExtrude","CAP_FACE",FACE,{"disambiguationData":[OSD([sQuery(id+"F0.wireOp",EDGE,"E0.bottom"),sQuery(id+"F0.wireOp",EDGE,"E0.top"),sQuery(id+"F0.wireOp",EDGE,"E0.left"),sQuery(id+"F0.wireOp",EDGE,"E0.right"),sQuery(id+"F0.wireOp",EDGE,"E2.bottom"),sQuery(id+"F0.wireOp",EDGE,"E2.top"),sQuery(id+"F0.wireOp",EDGE,"E2.left"),sQuery(id+"F0.wireOp",EDGE,"E2.right"),sQuery(id+"F0.wireOp",EDGE,"E3"),sQuery(id+"F0.wireOp",EDGE,"E4.MirrorC"),sQuery(id+"F0.wireOp",EDGE,"E5.MirrorC"),sQuery(id+"F0.wireOp",EDGE,"E6.MirrorC"),sQuery(id+"F0.wireOp",EDGE,"E7"),sQuery(id+"F0.wireOp",EDGE,"E8.MirrorC")])],"isStart":false}),makeQuery(id+"F3.opExtrude","SWEPT_FACE",FACE,{"disambiguationData":[OSD([sQuery(id+"F0.wireOp",EDGE,"E13")])]})]});
            var Q21;
            Q21=makeQuery(id+"F3.opExtrude","SWEPT_EDGE",EDGE,{"disambiguationData":[OSD([sQuery(id+"F0.wireOp",EDGE,"E2.left"),sQuery(id+"F0.wireOp",EDGE,"E11.MirrorC")])]});
            var Q22;
            {var subQ0=sQuery(id+"F0.wireOp",EDGE,"E11.MirrorC");var subQ1=sQuery(id+"F0.wireOp",EDGE,"E2.top");var subQ2=sQuery(id+"F0.wireOp",EDGE,"E2.left");Q22=makeQuery(id+"F3.boolean.opBoolean","INTERSECT",EDGE,{"derivedFrom":[makeQuery(id+"F1.opExtrude","CAP_FACE",FACE,{"disambiguationData":[OSD([sQuery(id+"F0.wireOp",EDGE,"E0.bottom"),sQuery(id+"F0.wireOp",EDGE,"E0.top"),sQuery(id+"F0.wireOp",EDGE,"E0.left"),sQuery(id+"F0.wireOp",EDGE,"E0.right"),sQuery(id+"F0.wireOp",EDGE,"E2.bottom"),subQ1,subQ2,sQuery(id+"F0.wireOp",EDGE,"E2.right"),sQuery(id+"F0.wireOp",EDGE,"E3"),sQuery(id+"F0.wireOp",EDGE,"E4.MirrorC"),sQuery(id+"F0.wireOp",EDGE,"E5.MirrorC"),sQuery(id+"F0.wireOp",EDGE,"E6.MirrorC"),sQuery(id+"F0.wireOp",EDGE,"E7"),sQuery(id+"F0.wireOp",EDGE,"E8.MirrorC")])],"isStart":false}),makeQuery(id+"F3.opExtrude","SWEPT_FACE",FACE,{"disambiguationData":[OSD([subQ0]),TDD([makeQuery(id+"F0.imprint","IMPRINT",EDGE,{"disambiguationData":[TD([[makeQuery(id+"F0.imprint","INTERSECT",VERTEX,{"derivedFrom":[subQ1,subQ0]}),1.0]])],"derivedFrom":subQ0})])]})]});}
            var Q23;
            Q23=makeQuery(id+"F3.boolean.opBoolean","INTERSECT",EDGE,{"derivedFrom":[makeQuery(id+"F1.opExtrude","CAP_FACE",FACE,{"disambiguationData":[OSD([sQuery(id+"F0.wireOp",EDGE,"E0.bottom"),sQuery(id+"F0.wireOp",EDGE,"E0.top"),sQuery(id+"F0.wireOp",EDGE,"E0.left"),sQuery(id+"F0.wireOp",EDGE,"E0.right"),sQuery(id+"F0.wireOp",EDGE,"E2.bottom"),sQuery(id+"F0.wireOp",EDGE,"E2.top"),sQuery(id+"F0.wireOp",EDGE,"E2.left"),sQuery(id+"F0.wireOp",EDGE,"E2.right"),sQuery(id+"F0.wireOp",EDGE,"E3"),sQuery(id+"F0.wireOp",EDGE,"E4.MirrorC"),sQuery(id+"F0.wireOp",EDGE,"E5.MirrorC"),sQuery(id+"F0.wireOp",EDGE,"E6.MirrorC"),sQuery(id+"F0.wireOp",EDGE,"E7"),sQuery(id+"F0.wireOp",EDGE,"E8.MirrorC")])],"isStart":false}),makeQuery(id+"F3.opExtrude","SWEPT_FACE",FACE,{"disambiguationData":[OSD([sQuery(id+"F0.wireOp",EDGE,"E14.MirrorC")])]})]});
            var Q24;
            Q24=makeQuery(id+"F3.opExtrude","SWEPT_EDGE",EDGE,{"disambiguationData":[OSD([sQuery(id+"F0.wireOp",EDGE,"E2.top"),sQuery(id+"F0.wireOp",EDGE,"E11.MirrorC")])]});
            var Q25;
            {var subQ0=sQuery(id+"F0.wireOp",EDGE,"E14.MirrorC");var subQ1=sQuery(id+"F0.wireOp",EDGE,"E2.top");Q25=makeQuery(id+"F3.opExtrude","SWEPT_EDGE",EDGE,{"disambiguationData":[OSD([subQ1,subQ0]),TDD([makeQuery(id+"F0.imprint","INTERSECT",VERTEX,{"disambiguationData":[OD(1.0)],"derivedFrom":[subQ1,subQ0]})])]});}
            var Q26;
            {var subQ0=sQuery(id+"F0.wireOp",EDGE,"E14.MirrorC");var subQ1=sQuery(id+"F0.wireOp",EDGE,"E2.top");Q26=makeQuery(id+"F3.opExtrude","SWEPT_EDGE",EDGE,{"disambiguationData":[OSD([subQ1,subQ0]),TDD([makeQuery(id+"F0.imprint","INTERSECT",VERTEX,{"disambiguationData":[OD(0.0)],"derivedFrom":[subQ1,subQ0]})])]});}
            var Q27;
            Q27=makeQuery(id+"F3.boolean.opBoolean","INTERSECT",EDGE,{"derivedFrom":[makeQuery(id+"F1.opExtrude","CAP_FACE",FACE,{"disambiguationData":[OSD([sQuery(id+"F0.wireOp",EDGE,"E0.bottom"),sQuery(id+"F0.wireOp",EDGE,"E0.top"),sQuery(id+"F0.wireOp",EDGE,"E0.left"),sQuery(id+"F0.wireOp",EDGE,"E0.right"),sQuery(id+"F0.wireOp",EDGE,"E2.bottom"),sQuery(id+"F0.wireOp",EDGE,"E2.top"),sQuery(id+"F0.wireOp",EDGE,"E2.left"),sQuery(id+"F0.wireOp",EDGE,"E2.right"),sQuery(id+"F0.wireOp",EDGE,"E3"),sQuery(id+"F0.wireOp",EDGE,"E4.MirrorC"),sQuery(id+"F0.wireOp",EDGE,"E5.MirrorC"),sQuery(id+"F0.wireOp",EDGE,"E6.MirrorC"),sQuery(id+"F0.wireOp",EDGE,"E7"),sQuery(id+"F0.wireOp",EDGE,"E8.MirrorC")])],"isStart":false}),makeQuery(id+"F3.opExtrude","SWEPT_FACE",FACE,{"disambiguationData":[OSD([sQuery(id+"F0.wireOp",EDGE,"E9")])]})]});
            fillet(context, id + "F4", {"entities" : qUnion([Q0, Q1, Q2, Q3, Q4, Q5, Q6, Q7, Q8, Q9, Q10, Q11, Q12, Q13, Q14, Q15, Q16, Q17, Q18, Q19, Q20, Q21, Q22, Q23, Q24, Q25, Q26, Q27]), "radius" : 2 * mm, "tangentPropagation" : true, "allowEdgeOverflow" : false});
        }
        {
            var Q0;
            Q0=sQuery(id+"F0.wireOp",VERTEX,"E5.MirrorC.center");
            var Q1;
            Q1=sQuery(id+"F0.wireOp",VERTEX,"E3.center");
            var Q2;
            Q2=sQuery(id+"F0.wireOp",VERTEX,"E7.center");
            var Q3;
            Q3=sQuery(id+"F0.wireOp",VERTEX,"E4.MirrorC.center");
            var Q4;
            Q4=sQuery(id+"F0.wireOp",VERTEX,"E8.MirrorC.center");
            var Q5;
            Q5=sQuery(id+"F0.wireOp",VERTEX,"E6.MirrorC.center");
            var Q6;
            Q6=makeQuery(id+"F1.opExtrude","SWEPT_BODY",BODY,{"disambiguationData":[OSD([sQuery(id+"F0.wireOp",EDGE,"E0.bottom"),sQuery(id+"F0.wireOp",EDGE,"E0.top"),sQuery(id+"F0.wireOp",EDGE,"E0.left"),sQuery(id+"F0.wireOp",EDGE,"E0.right"),sQuery(id+"F0.wireOp",EDGE,"E2.bottom"),sQuery(id+"F0.wireOp",EDGE,"E2.top"),sQuery(id+"F0.wireOp",EDGE,"E2.left"),sQuery(id+"F0.wireOp",EDGE,"E2.right"),sQuery(id+"F0.wireOp",EDGE,"E3"),sQuery(id+"F0.wireOp",EDGE,"E4.MirrorC"),sQuery(id+"F0.wireOp",EDGE,"E5.MirrorC"),sQuery(id+"F0.wireOp",EDGE,"E6.MirrorC"),sQuery(id+"F0.wireOp",EDGE,"E7"),sQuery(id+"F0.wireOp",EDGE,"E8.MirrorC")])]});
            hole(context, id + "F5", {"style" : HoleStyle.C_SINK, "endStyle" : HoleEndStyle.BLIND, "oppositeDirection" : true, "holeDiameter" : 3.5 * mm, "cSinkDiameter" : 6.5 * mm, "cSinkAngle" : 90 * degree, "majorDiameter" : 5 * mm, "holeDepth" : 5 * mm, "isTappedThrough" : true, "tappedDepth" : 12 * mm, "tapClearance" : 3, "locations" : qUnion([Q0, Q1, Q2, Q3, Q4, Q5]), "scope" : qUnion([Q6]), "startStyle" : HoleStartStyle.SKETCH});
        }
    });
